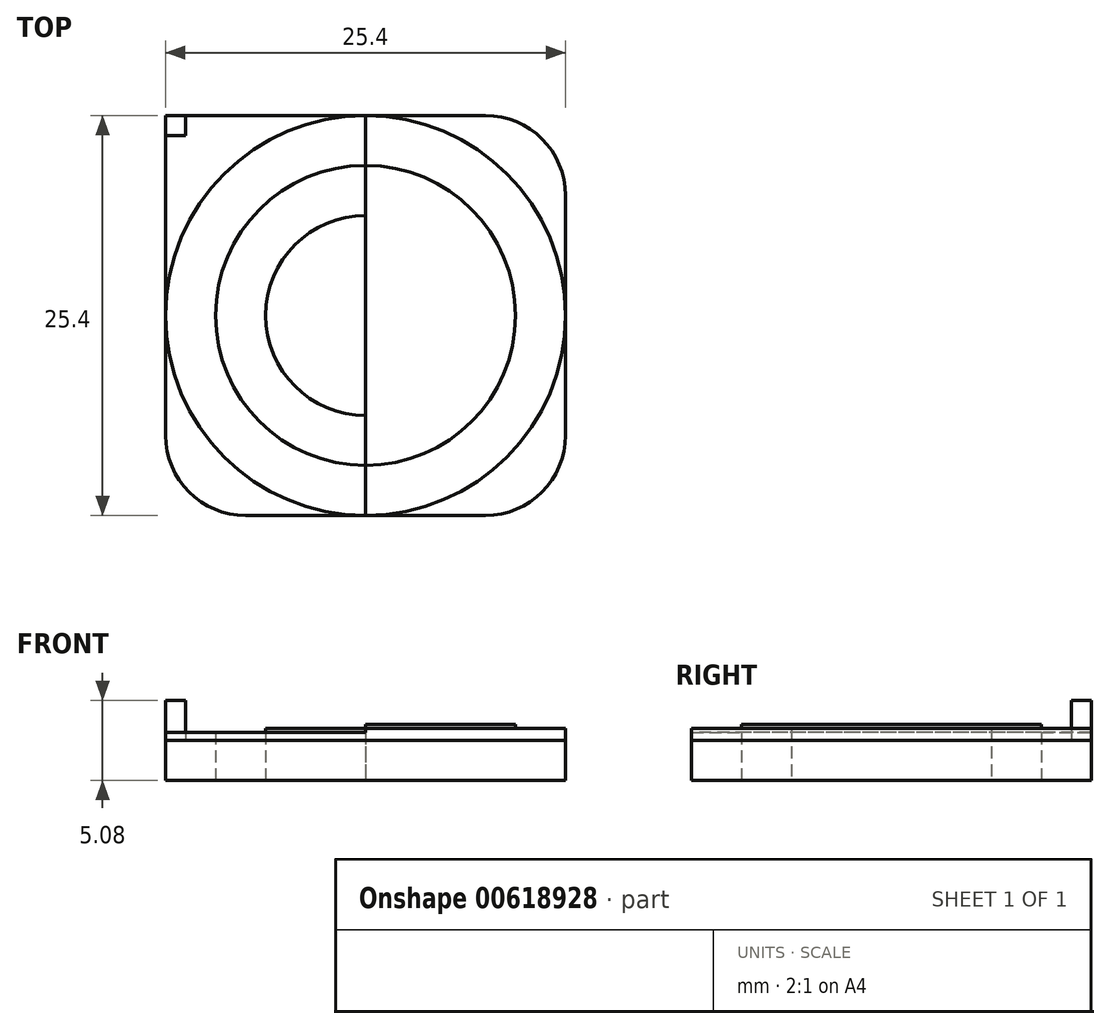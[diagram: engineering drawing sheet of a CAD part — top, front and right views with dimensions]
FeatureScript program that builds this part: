
annotation { "Feature Type Name" : "Feature", "Feature Type Description" : "" }
export const myFeature = defineFeature(function(context is Context, id is Id, definition is map)
    precondition{}
    {
        {
            var Q0;
            Q0=qCreatedBy(makeId("Top.planeOp"),FACE);
            var sketch = newSketch(context, id + "F0", { "sketchPlane" : qUnion([Q0])});
            skLineSegment(sketch, "E0", {"start": v(0, 0) * mm, "end": v(0, 25.4) * mm});
            skLineSegment(sketch, "E1", {"start": v(0, 25.4) * mm, "end": v(25.4, 25.4) * mm});
            skLineSegment(sketch, "E2", {"start": v(25.4, 25.4) * mm, "end": v(25.4, 0) * mm});
            skLineSegment(sketch, "E3", {"start": v(25.4, 0) * mm, "end": v(0, 0) * mm});
            skLineSegment(sketch, "E4", {"start": v(0, 12.7) * mm, "end": v(25.4, 12.7) * mm});
            skLineSegment(sketch, "E5", {"start": v(12.7, 25.4) * mm, "end": v(12.7, 0) * mm});
            skCircle(sketch, "E6", {"center": v(12.7, 12.7) * mm, "radius": 6.35 * mm});
            skCircle(sketch, "E7", {"center": v(12.7, 12.7) * mm, "radius": 9.53 * mm});
            skCircle(sketch, "E8", {"center": v(12.7, 12.7) * mm, "radius": 12.7 * mm});
            skLineSegment(sketch, "E9", {"start": v(0, 24.13) * mm, "end": v(1.27, 24.13) * mm});
            skLineSegment(sketch, "E10", {"start": v(1.27, 24.13) * mm, "end": v(1.27, 25.4) * mm});
            skSolve(sketch);
        }
        {
            var Q0;
            {var subQ0=sQuery(id+"F0.wireOp",EDGE,"E3");var subQ1=sQuery(id+"F0.wireOp",EDGE,"E0");var subQ2=makeQuery(id+"F0.imprint","INTERSECT",VERTEX,{"derivedFrom":[subQ1,subQ0]});Q0=makeQuery(id+"F0.imprint","IMPRINT",FACE,{"disambiguationData":[TD([[makeQuery(id+"F0.imprint","IMPRINT",EDGE,{"disambiguationData":[TD([[subQ2,-1.0]])],"derivedFrom":subQ1}),-1.0]])]});}
            var Q1;
            {var subQ0=sQuery(id+"F0.wireOp",EDGE,"E1");var subQ1=sQuery(id+"F0.wireOp",EDGE,"E0");var subQ2=makeQuery(id+"F0.imprint","INTERSECT",VERTEX,{"derivedFrom":[subQ1,subQ0]});Q1=makeQuery(id+"F0.imprint","IMPRINT",FACE,{"disambiguationData":[TD([[makeQuery(id+"F0.imprint","IMPRINT",EDGE,{"disambiguationData":[TD([[subQ2,1.0]])],"derivedFrom":subQ1}),-1.0]])]});}
            var Q2;
            {var subQ0=sQuery(id+"F0.wireOp",EDGE,"E2");var subQ1=sQuery(id+"F0.wireOp",EDGE,"E1");var subQ2=makeQuery(id+"F0.imprint","INTERSECT",VERTEX,{"derivedFrom":[subQ1,subQ0]});Q2=makeQuery(id+"F0.imprint","IMPRINT",FACE,{"disambiguationData":[TD([[makeQuery(id+"F0.imprint","IMPRINT",EDGE,{"disambiguationData":[TD([[subQ2,1.0]])],"derivedFrom":subQ1}),-1.0]])]});}
            var Q3;
            {var subQ0=sQuery(id+"F0.wireOp",EDGE,"E3");var subQ1=sQuery(id+"F0.wireOp",EDGE,"E2");var subQ2=makeQuery(id+"F0.imprint","INTERSECT",VERTEX,{"derivedFrom":[subQ1,subQ0]});Q3=makeQuery(id+"F0.imprint","IMPRINT",FACE,{"disambiguationData":[TD([[makeQuery(id+"F0.imprint","IMPRINT",EDGE,{"disambiguationData":[TD([[subQ2,1.0]])],"derivedFrom":subQ1}),-1.0]])]});}
            var Q4;
            {var subQ0=sQuery(id+"F0.wireOp",EDGE,"E9");Q4=makeQuery(id+"F0.imprint","IMPRINT",FACE,{"disambiguationData":[TD([[makeQuery(id+"F0.imprint","IMPRINT",EDGE,{"derivedFrom":subQ0}),-1.0]])]});}
            extrude(context, id + "F1", {"entities" : qUnion([Q0, Q1, Q2, Q3, Q4]), "depth" : 2.54 * mm, "offsetDistance" : 25.4 * mm});
        }
        {
            var Q0;
            {var subQ1=sQuery(id+"F0.wireOp",EDGE,"E4");var subQ3=sQuery(id+"F0.wireOp",EDGE,"E7");var subQ4=makeQuery(id+"F0.imprint","INTERSECT",VERTEX,{"disambiguationData":[OD(0.0)],"derivedFrom":[subQ1,subQ3]});Q0=makeQuery(id+"F0.imprint","IMPRINT",FACE,{"disambiguationData":[TD([[makeQuery(id+"F0.imprint","IMPRINT",EDGE,{"disambiguationData":[TD([[subQ4,-1.0]])],"derivedFrom":subQ3}),-1.0]])]});}
            var Q1;
            {var subQ1=sQuery(id+"F0.wireOp",EDGE,"E4");var subQ3=sQuery(id+"F0.wireOp",EDGE,"E7");var subQ4=makeQuery(id+"F0.imprint","INTERSECT",VERTEX,{"disambiguationData":[OD(1.0)],"derivedFrom":[subQ1,subQ3]});Q1=makeQuery(id+"F0.imprint","IMPRINT",FACE,{"disambiguationData":[TD([[makeQuery(id+"F0.imprint","IMPRINT",EDGE,{"disambiguationData":[TD([[subQ4,-1.0]])],"derivedFrom":subQ3}),-1.0]])]});}
            var Q2;
            {var subQ1=sQuery(id+"F0.wireOp",EDGE,"E4");var subQ3=sQuery(id+"F0.wireOp",EDGE,"E7");var subQ4=makeQuery(id+"F0.imprint","INTERSECT",VERTEX,{"disambiguationData":[OD(1.0)],"derivedFrom":[subQ1,subQ3]});Q2=makeQuery(id+"F0.imprint","IMPRINT",FACE,{"disambiguationData":[TD([[makeQuery(id+"F0.imprint","IMPRINT",EDGE,{"disambiguationData":[TD([[subQ4,1.0]])],"derivedFrom":subQ3}),-1.0]])]});}
            var Q3;
            {var subQ1=sQuery(id+"F0.wireOp",EDGE,"E4");var subQ3=sQuery(id+"F0.wireOp",EDGE,"E7");var subQ4=makeQuery(id+"F0.imprint","INTERSECT",VERTEX,{"disambiguationData":[OD(0.0)],"derivedFrom":[subQ1,subQ3]});Q3=makeQuery(id+"F0.imprint","IMPRINT",FACE,{"disambiguationData":[TD([[makeQuery(id+"F0.imprint","IMPRINT",EDGE,{"disambiguationData":[TD([[subQ4,1.0]])],"derivedFrom":subQ3}),-1.0]])]});}
            extrude(context, id + "F2", {"entities" : qUnion([Q0, Q1, Q2, Q3]), "operationType" : NewBodyOperationType.ADD, "depth" : 3.05 * mm, "offsetDistance" : 25.4 * mm});
        }
        {
            var Q0;
            {var subQ3=sQuery(id+"F0.wireOp",EDGE,"E9");Q0=makeQuery(id+"F0.imprint","IMPRINT",FACE,{"disambiguationData":[TD([[makeQuery(id+"F0.imprint","IMPRINT",EDGE,{"derivedFrom":subQ3}),1.0]])]});}
            extrude(context, id + "F3", {"entities" : qUnion([Q0]), "operationType" : NewBodyOperationType.ADD, "depth" : 5.08 * mm, "offsetDistance" : 25.4 * mm});
        }
        {
            var Q0;
            {var subQ0=sQuery(id+"F0.wireOp",EDGE,"E7");var subQ1=sQuery(id+"F0.wireOp",EDGE,"E4");var subQ2=makeQuery(id+"F0.imprint","INTERSECT",VERTEX,{"disambiguationData":[OD(0.0)],"derivedFrom":[subQ1,subQ0]});Q0=makeQuery(id+"F0.imprint","IMPRINT",FACE,{"disambiguationData":[TD([[makeQuery(id+"F0.imprint","IMPRINT",EDGE,{"disambiguationData":[TD([[subQ2,-1.0]])],"derivedFrom":subQ1}),1.0]])]});}
            var Q1;
            {var subQ0=sQuery(id+"F0.wireOp",EDGE,"E6");var subQ1=sQuery(id+"F0.wireOp",EDGE,"E4");var subQ2=makeQuery(id+"F0.imprint","INTERSECT",VERTEX,{"disambiguationData":[OD(1.0)],"derivedFrom":[subQ1,subQ0]});Q1=makeQuery(id+"F0.imprint","IMPRINT",FACE,{"disambiguationData":[TD([[makeQuery(id+"F0.imprint","IMPRINT",EDGE,{"disambiguationData":[TD([[subQ2,-1.0]])],"derivedFrom":subQ1}),1.0]])]});}
            var Q2;
            {var subQ0=sQuery(id+"F0.wireOp",EDGE,"E7");var subQ1=sQuery(id+"F0.wireOp",EDGE,"E4");var subQ2=makeQuery(id+"F0.imprint","INTERSECT",VERTEX,{"disambiguationData":[OD(0.0)],"derivedFrom":[subQ1,subQ0]});Q2=makeQuery(id+"F0.imprint","IMPRINT",FACE,{"disambiguationData":[TD([[makeQuery(id+"F0.imprint","IMPRINT",EDGE,{"disambiguationData":[TD([[subQ2,-1.0]])],"derivedFrom":subQ1}),-1.0]])]});}
            var Q3;
            {var subQ0=sQuery(id+"F0.wireOp",EDGE,"E6");var subQ1=sQuery(id+"F0.wireOp",EDGE,"E4");var subQ2=makeQuery(id+"F0.imprint","INTERSECT",VERTEX,{"disambiguationData":[OD(1.0)],"derivedFrom":[subQ1,subQ0]});Q3=makeQuery(id+"F0.imprint","IMPRINT",FACE,{"disambiguationData":[TD([[makeQuery(id+"F0.imprint","IMPRINT",EDGE,{"disambiguationData":[TD([[subQ2,-1.0]])],"derivedFrom":subQ1}),-1.0]])]});}
            extrude(context, id + "F4", {"entities" : qUnion([Q0, Q1, Q2, Q3]), "operationType" : NewBodyOperationType.ADD, "depth" : 3.3 * mm, "offsetDistance" : 25.4 * mm});
        }
        {
            var Q0;
            {var subQ0=sQuery(id+"F0.wireOp",EDGE,"E6");var subQ1=sQuery(id+"F0.wireOp",EDGE,"E4");var subQ2=makeQuery(id+"F0.imprint","INTERSECT",VERTEX,{"disambiguationData":[OD(0.0)],"derivedFrom":[subQ1,subQ0]});Q0=makeQuery(id+"F0.imprint","IMPRINT",FACE,{"disambiguationData":[TD([[makeQuery(id+"F0.imprint","IMPRINT",EDGE,{"disambiguationData":[TD([[subQ2,-1.0]])],"derivedFrom":subQ1}),1.0]])]});}
            var Q1;
            {var subQ0=sQuery(id+"F0.wireOp",EDGE,"E6");var subQ1=sQuery(id+"F0.wireOp",EDGE,"E4");var subQ2=makeQuery(id+"F0.imprint","INTERSECT",VERTEX,{"disambiguationData":[OD(0.0)],"derivedFrom":[subQ1,subQ0]});Q1=makeQuery(id+"F0.imprint","IMPRINT",FACE,{"disambiguationData":[TD([[makeQuery(id+"F0.imprint","IMPRINT",EDGE,{"disambiguationData":[TD([[subQ2,-1.0]])],"derivedFrom":subQ1}),-1.0]])]});}
            var Q2;
            {var subQ0=sQuery(id+"F0.wireOp",EDGE,"E5");var subQ1=sQuery(id+"F0.wireOp",EDGE,"E4");var subQ2=makeQuery(id+"F0.imprint","INTERSECT",VERTEX,{"derivedFrom":[subQ1,subQ0]});Q2=makeQuery(id+"F0.imprint","IMPRINT",FACE,{"disambiguationData":[TD([[makeQuery(id+"F0.imprint","IMPRINT",EDGE,{"disambiguationData":[TD([[subQ2,-1.0]])],"derivedFrom":subQ1}),1.0]])]});}
            var Q3;
            {var subQ0=sQuery(id+"F0.wireOp",EDGE,"E5");var subQ1=sQuery(id+"F0.wireOp",EDGE,"E4");var subQ2=makeQuery(id+"F0.imprint","INTERSECT",VERTEX,{"derivedFrom":[subQ1,subQ0]});Q3=makeQuery(id+"F0.imprint","IMPRINT",FACE,{"disambiguationData":[TD([[makeQuery(id+"F0.imprint","IMPRINT",EDGE,{"disambiguationData":[TD([[subQ2,-1.0]])],"derivedFrom":subQ1}),-1.0]])]});}
            extrude(context, id + "F5", {"entities" : qUnion([Q0, Q1, Q2, Q3]), "operationType" : NewBodyOperationType.ADD, "depth" : 3.56 * mm, "offsetDistance" : 25.4 * mm});
        }
        {
            var Q0;
            Q0=makeQuery(id+"F1.opExtrude","SWEPT_EDGE",EDGE,{"disambiguationData":[OSD([sQuery(id+"F0.wireOp",EDGE,"E0"),sQuery(id+"F0.wireOp",EDGE,"E3")])]});
            var Q1;
            Q1=makeQuery(id+"F1.opExtrude","SWEPT_EDGE",EDGE,{"disambiguationData":[OSD([sQuery(id+"F0.wireOp",EDGE,"E1"),sQuery(id+"F0.wireOp",EDGE,"E2")])]});
            var Q2;
            Q2=makeQuery(id+"F1.opExtrude","SWEPT_EDGE",EDGE,{"disambiguationData":[OSD([sQuery(id+"F0.wireOp",EDGE,"E2"),sQuery(id+"F0.wireOp",EDGE,"E3")])]});
            fillet(context, id + "F6", {"entities" : qUnion([Q0, Q1, Q2]), "radius" : 5.08 * mm, "tangentPropagation" : true, "allowEdgeOverflow" : false});
        }
    });
